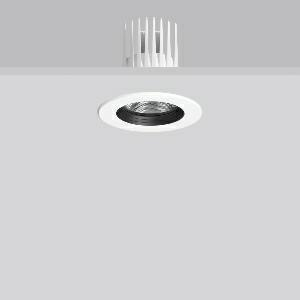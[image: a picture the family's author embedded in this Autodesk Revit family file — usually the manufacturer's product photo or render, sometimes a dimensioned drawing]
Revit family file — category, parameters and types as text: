
# Revit family: heledon_mini_e_901741_002_3bdc
name_source: partatom
category: Lighting Fixtures
units: mm (PartAtom-declared; Revit-internal decimal feet)

## family parameters
Cut with Voids When Loaded = No
Host = Face
Light Source = No
Part Type = Normal
Room Calculation Point = No
Round Connector Dimension = Use Diameter
Shared = No

## types (1)
- HELEDON mini E (1 x LED Modul 930, 2450 lm, 3000)
    Apparent Load = 20 VA
    Approval mark = CE
    CIE Flux Codes = 99 100 100 100 100
    Color Rendering = 90
    Color Temperature = 3000
    Default Elevation = 1800 mm
    Description = Series: HELEDON mini
Round recessed downlight. Housing: die-cast aluminium, powder-coated. Black plastic ring and recessed LED to prevent glare from the side. Optical assembly with reflector made of MIRO-Silver with 98% total light reflection for outstanding efficiency - can be changed without tools. Best colour rendering index Ra>90. Suitable for Recessed ceiling mounting. Installation without tools thanks to spring fastening system. Including separate LED converter with connecting cable 600 mm.High quality converter without flickering and stroboscopic effect. Through-wiring box (5 pole) available as accessory. The following accessories can be mounted without use of tools: interchangeable lenses, decorative glasses, honeycomb louvre, clear and frosted diffusers, white interchangeable plastic ring. 
Colour: traffic white, matt (RAL 9016)
Diameter: 124 mm
Height: 3 mm
Cut-out diameter: 114 mm
Recess height: 170 mm
Luminaire: recess height: 120 mm
Lamp: LED
Socket: without socket
Colour temperature: 3000K
Colour rendering index (CRI): 92
System power: 20 W
Rated luminous flux: 2450 lm
Luminous efficiency: 123 lm/W
Control gear: Regulated power supply
Protection class: II
Type of protection: IP 20
    Height = 0 mm  [stored 0 ft]
    Lamp = 1 x LED Modul 930
    Lamp Light Flux = 2450 lm
    Lamp count = 1
    Length = 124 mm  [stored 0.406824 ft]
    Lifetime = 50000 h
    Luminous efficacy = 123 lm/W
    Manufacturer = RZB
    ModVariant = No
    Model = 901741.002
    Mounting Place = Ceiling
    Mounting Type = Recessed
    Number of Poles = 1
    OnlyDefault = Yes
    Power Factor = 1
    Product Name = HELEDON mini E
    Product group = Recessed downlights
    ProductGroupID = 402
    Protection Class = Protection class II
    Protection Degree = IP 20
    RLX_Detail_Level = 1
    RLX_Emergency_Light_Flux = 0 lm
    RLX_Emergency_Type = 0
    RLX_Emergency_Type_DB = No
    RlxData = <blob elided: 125861 chars, md5=6c34db48>
    Socket = socket
    Standby Power = 0 W
    System Light Flux = 2450 lm
    System Power = 20 W
    Type Comments = Product without accessories
    Type Image = 901657.002.jpg
    URL = http://relux.com
    VarID = ---
    Voltage = 230 V
    Voltage Range = 220-240 V
    Weight = 0.00 kg
    Width = 0 mm  [stored 0 ft]

note: [stored X ft] marks values corroborated as IEEE doubles in the binary element streams (Revit-internal decimal feet)

## geometry (parser evidence)
native form markers: Blend x4, Sweep x12
no freeform markers — native parametric forms only
